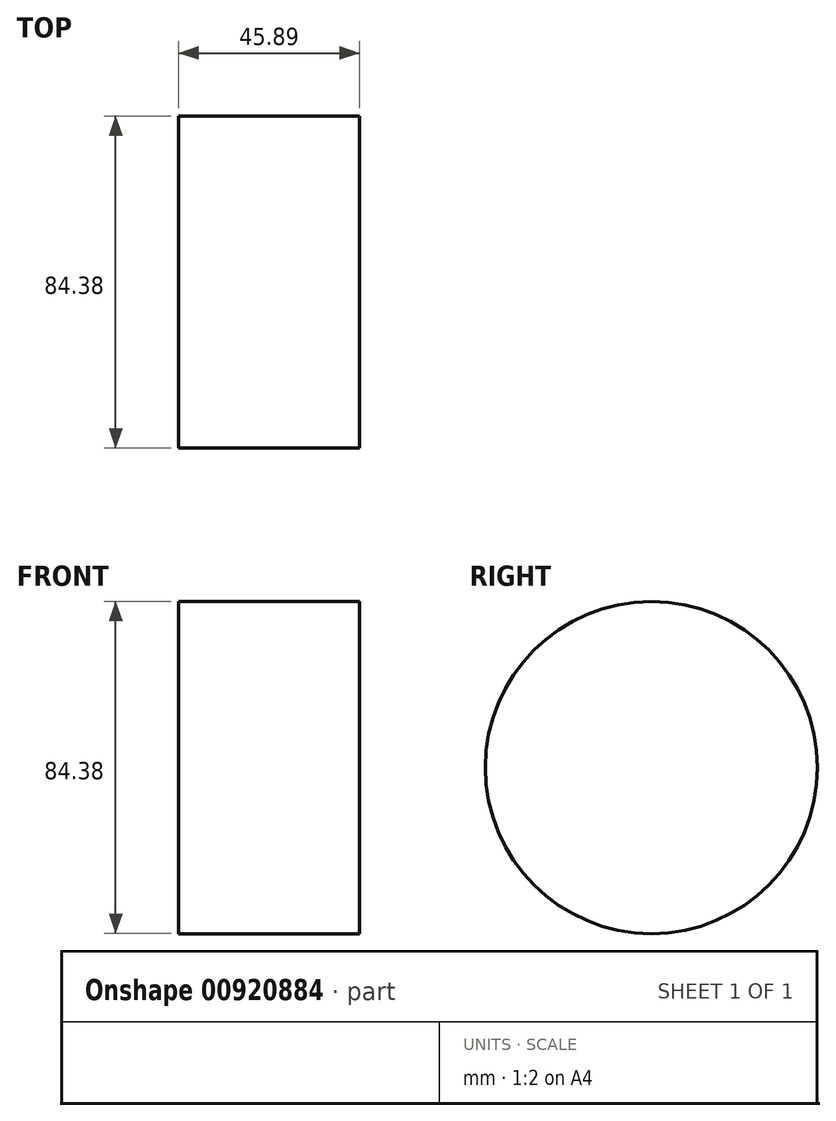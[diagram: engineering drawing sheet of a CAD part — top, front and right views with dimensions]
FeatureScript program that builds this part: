
annotation { "Feature Type Name" : "Feature", "Feature Type Description" : "" }
export const myFeature = defineFeature(function(context is Context, id is Id, definition is map)
    precondition{}
    {
        {
            var Q0;
            Q0=qCreatedBy(makeId("Front.planeOp"),FACE);
            var sketch = newSketch(context, id + "F0", { "sketchPlane" : qUnion([Q0])});
            skLineSegment(sketch, "E0.bottom", {"start": v(0, 0) * mm, "end": v(45.9, 0) * mm});
            skLineSegment(sketch, "E0.top", {"start": v(0, 42.2) * mm, "end": v(45.9, 42.2) * mm});
            skLineSegment(sketch, "E0.left", {"start": v(0, 0) * mm, "end": v(0, 42.2) * mm});
            skLineSegment(sketch, "E0.right", {"start": v(45.9, 0) * mm, "end": v(45.9, 42.2) * mm});
            skLineSegment(sketch, "E1.top", {"start": v(0, 64.22) * mm, "end": v(45.9, 64.22) * mm});
            skLineSegment(sketch, "E1.left", {"start": v(0, 42.2) * mm, "end": v(0, 64.22) * mm});
            skLineSegment(sketch, "E1.right", {"start": v(45.9, 42.2) * mm, "end": v(45.9, 64.22) * mm});
            skLineSegment(sketch, "E2", {"start": v(0, 53.2) * mm, "end": v(45.9, 53.2) * mm});
            skSolve(sketch);
        }
        {
            var Q0;
            Q0=makeQuery(id+"F0.imprint","IMPRINT",FACE,{"disambiguationData":[TD([[makeQuery(id+"F0.imprint","IMPRINT",EDGE,{"derivedFrom":sQuery(id+"F0.wireOp",EDGE,"E0.bottom")}),1.0]])]});
            var Q1;
            Q1=sQuery(id+"F0.wireOp",EDGE,"E0.bottom");
            revolve(context, id + "F1", {"surfaceOperationType" : NewSurfaceOperationType.NEW, "entities" : qUnion([Q0]), "axis" : qUnion([Q1]), "revolveType" : RevolveType.FULL});
        }
        {
            var Q0;
            Q0=sQuery(id+"F0.wireOp",EDGE,"E1.right");
            var Q1;
            Q1=sQuery(id+"F0.wireOp",EDGE,"E1.top");
            var Q2;
            Q2=sQuery(id+"F0.wireOp",EDGE,"E1.left");
            var Q3;
            Q3=sQuery(id+"F0.wireOp",EDGE,"E0.bottom");
            revolve(context, id + "F2", {"bodyType" : ToolBodyType.SURFACE, "surfaceOperationType" : NewSurfaceOperationType.NEW, "surfaceEntities" : qUnion([Q0, Q1, Q2]), "axis" : qUnion([Q3]), "revolveType" : RevolveType.FULL});
        }
        {
            var Q0;
            Q0=sQuery(id+"F0.wireOp",EDGE,"E2");
            var Q1;
            Q1=sQuery(id+"F0.wireOp",EDGE,"E0.bottom");
            revolve(context, id + "F3", {"bodyType" : ToolBodyType.SURFACE, "surfaceOperationType" : NewSurfaceOperationType.NEW, "surfaceEntities" : qUnion([Q0]), "axis" : qUnion([Q1]), "revolveType" : RevolveType.FULL});
        }
    });
